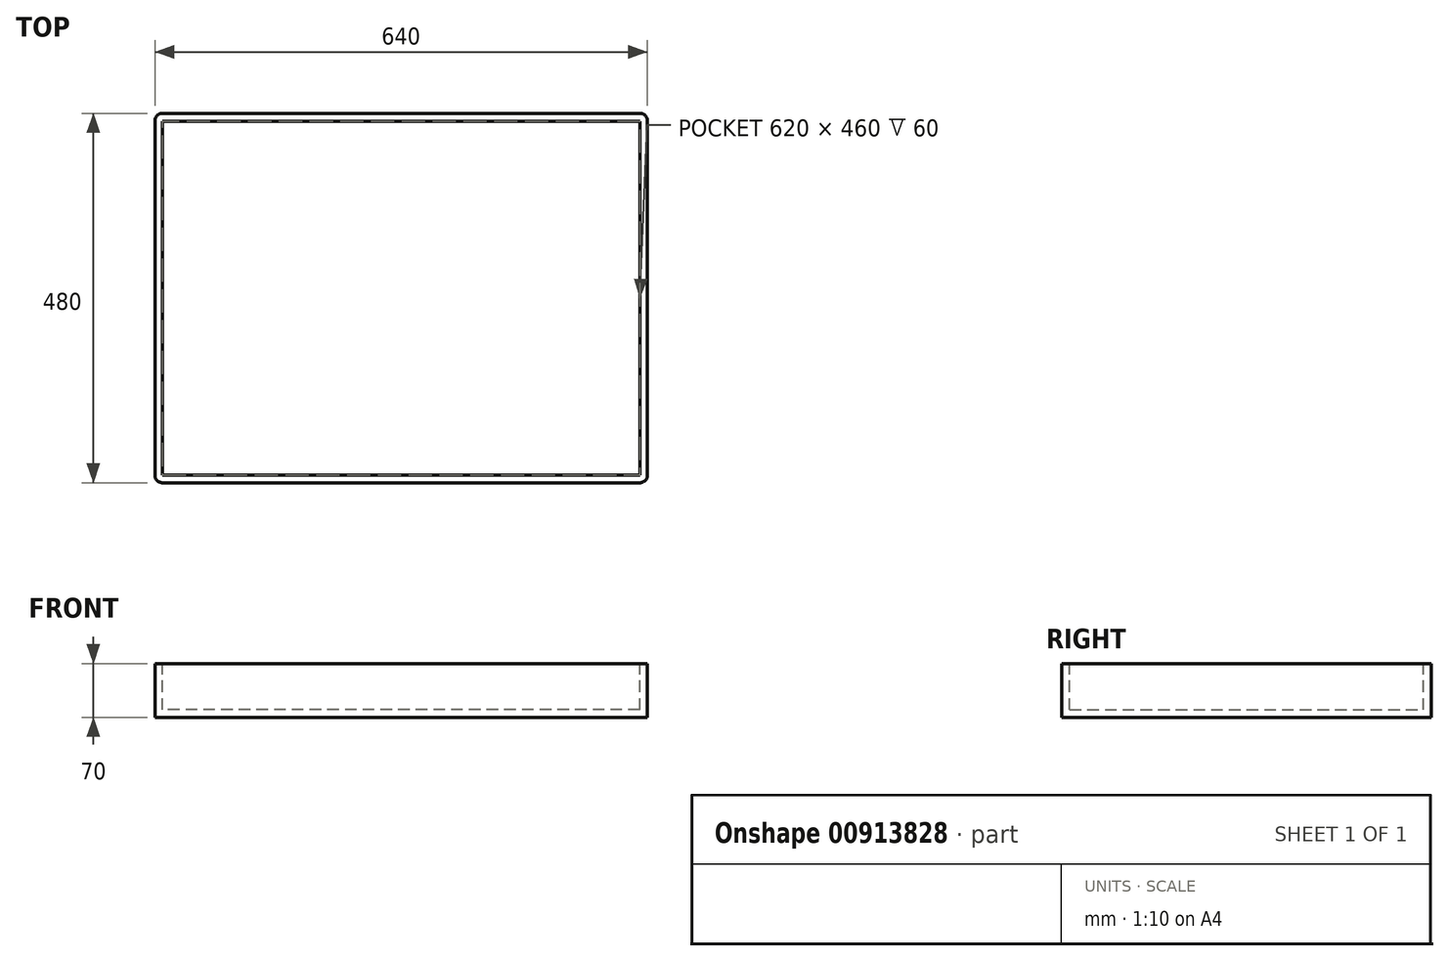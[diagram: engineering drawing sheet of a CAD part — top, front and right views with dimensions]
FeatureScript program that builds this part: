
annotation { "Feature Type Name" : "Feature", "Feature Type Description" : "" }
export const myFeature = defineFeature(function(context is Context, id is Id, definition is map)
    precondition{}
    {
        {
            var Q0;
            Q0=qCreatedBy(makeId("Top.planeOp"),FACE);
            var sketch = newSketch(context, id + "F0", { "sketchPlane" : qUnion([Q0])});
            skLineSegment(sketch, "E0.bottom", {"start": v(310, -230) * mm, "end": v(-310, -230) * mm});
            skLineSegment(sketch, "E0.top", {"start": v(310, 230) * mm, "end": v(-310, 230) * mm});
            skLineSegment(sketch, "E0.left", {"start": v(310, -230) * mm, "end": v(310, 230) * mm});
            skLineSegment(sketch, "E0.right", {"start": v(-310, -230) * mm, "end": v(-310, 230) * mm});
            skPoint(sketch, "E0.middle", {"position": v(0, 0) * mm});
            skLineSegment(sketch, "E1.bottom", {"start": v(320, -240) * mm, "end": v(-320, -240) * mm});
            skLineSegment(sketch, "E1.top", {"start": v(320, 240) * mm, "end": v(-320, 240) * mm});
            skLineSegment(sketch, "E1.left", {"start": v(320, -240) * mm, "end": v(320, 240) * mm});
            skLineSegment(sketch, "E1.right", {"start": v(-320, -240) * mm, "end": v(-320, 240) * mm});
            skSolve(sketch);
        }
        {
            var Q0;
            Q0=makeQuery(id+"F0.imprint","IMPRINT",FACE,{"disambiguationData":[TD([[makeQuery(id+"F0.imprint","IMPRINT",EDGE,{"derivedFrom":sQuery(id+"F0.wireOp",EDGE,"E0.bottom")}),1.0]])]});
            var Q1;
            Q1=makeQuery(id+"F0.imprint","IMPRINT",FACE,{"disambiguationData":[TD([[makeQuery(id+"F0.imprint","IMPRINT",EDGE,{"derivedFrom":sQuery(id+"F0.wireOp",EDGE,"E0.bottom")}),-1.0]])]});
            extrude(context, id + "F1", {"entities" : qUnion([Q0, Q1]), "oppositeDirection" : true, "depth" : 70 * mm, "offsetDistance" : 25 * mm});
        }
        {
            var Q0;
            Q0=makeQuery(id+"F0.imprint","IMPRINT",FACE,{"disambiguationData":[TD([[makeQuery(id+"F0.imprint","IMPRINT",EDGE,{"derivedFrom":sQuery(id+"F0.wireOp",EDGE,"E0.bottom")}),-1.0]])]});
            extrude(context, id + "F2", {"entities" : qUnion([Q0]), "operationType" : NewBodyOperationType.REMOVE, "oppositeDirection" : true, "depth" : 60 * mm, "offsetDistance" : 25 * mm});
        }
        {
            var Q0;
            Q0=makeQuery(id+"F1.opExtrude","SWEPT_EDGE",EDGE,{"disambiguationData":[OSD([sQuery(id+"F0.wireOp",EDGE,"E1.bottom"),sQuery(id+"F0.wireOp",EDGE,"E1.left")])]});
            var Q1;
            Q1=makeQuery(id+"F1.opExtrude","SWEPT_EDGE",EDGE,{"disambiguationData":[OSD([sQuery(id+"F0.wireOp",EDGE,"E1.top"),sQuery(id+"F0.wireOp",EDGE,"E1.left")])]});
            var Q2;
            Q2=makeQuery(id+"F1.opExtrude","SWEPT_EDGE",EDGE,{"disambiguationData":[OSD([sQuery(id+"F0.wireOp",EDGE,"E1.bottom"),sQuery(id+"F0.wireOp",EDGE,"E1.right")])]});
            var Q3;
            Q3=makeQuery(id+"F1.opExtrude","SWEPT_EDGE",EDGE,{"disambiguationData":[OSD([sQuery(id+"F0.wireOp",EDGE,"E1.top"),sQuery(id+"F0.wireOp",EDGE,"E1.right")])]});
            fillet(context, id + "F3", {"entities" : qUnion([Q0, Q1, Q2, Q3]), "radius" : 10 * mm, "tangentPropagation" : true, "allowEdgeOverflow" : false});
        }
    });
